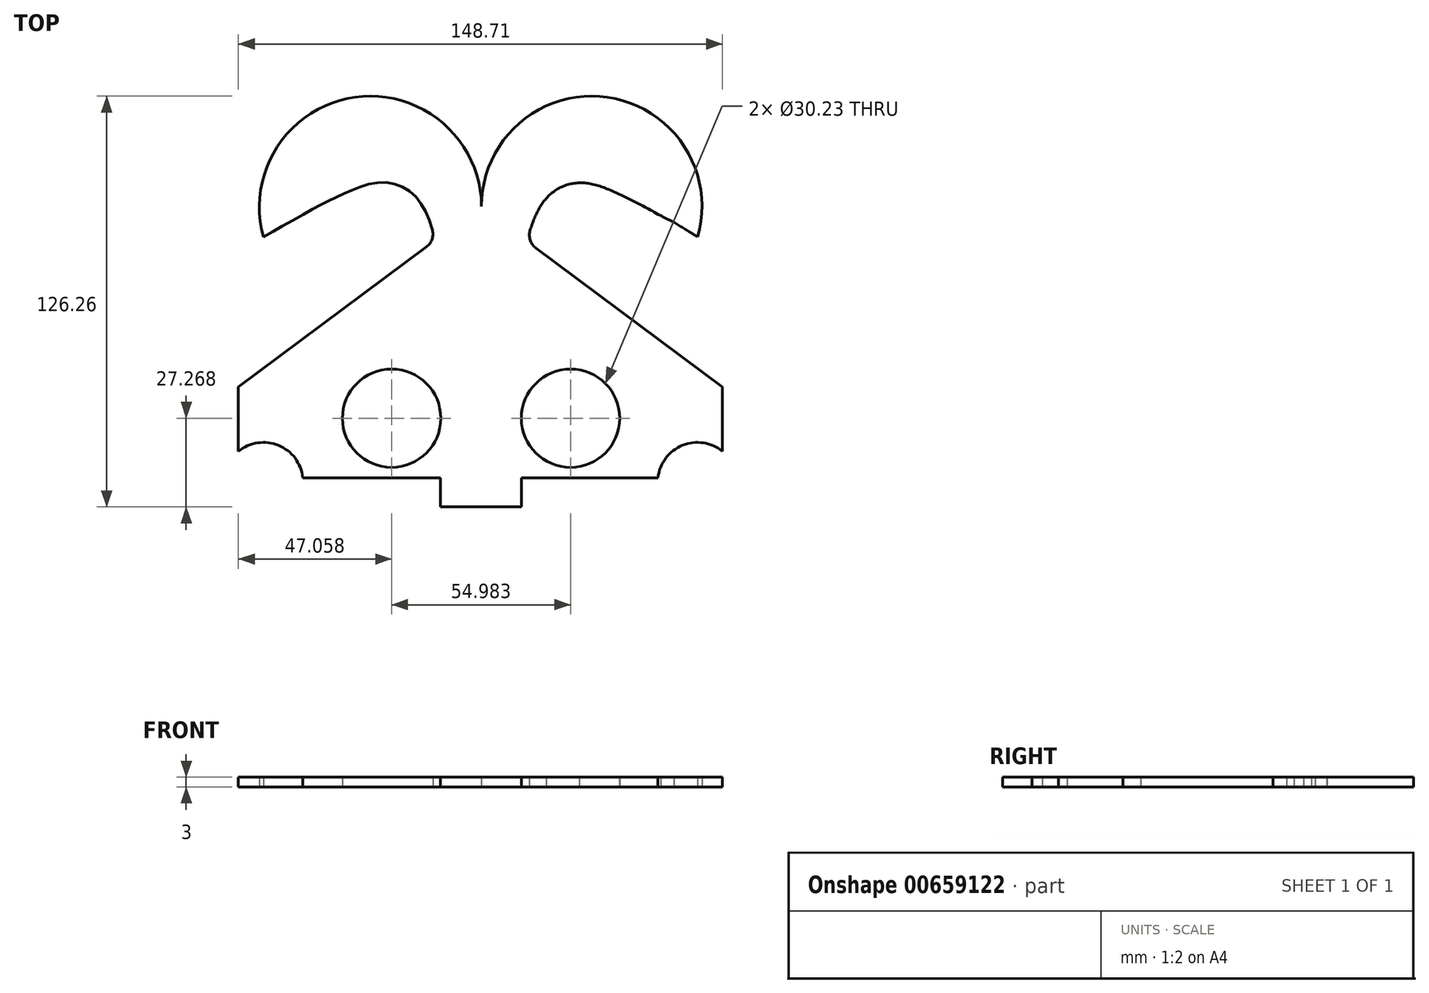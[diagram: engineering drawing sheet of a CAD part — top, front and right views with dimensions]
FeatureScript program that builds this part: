
annotation { "Feature Type Name" : "Feature", "Feature Type Description" : "" }
export const myFeature = defineFeature(function(context is Context, id is Id, definition is map)
    precondition{}
    {
        {
            var Q0;
            Q0=qCreatedBy(makeId("Top.planeOp"),FACE);
            var sketch = newSketch(context, id + "F0", { "sketchPlane" : qUnion([Q0])});
            skLineSegment(sketch, "E0", {"start": v(-16.81, 42.98) * mm, "end": v(-74.55, 0) * mm});
            skLineSegment(sketch, "E1", {"start": v(-74.55, 0) * mm, "end": v(-74.55, -19.8) * mm});
            skLineSegment(sketch, "E2", {"start": v(-54.75, -27.9) * mm, "end": v(0, -27.9) * mm});
            skLineSegment(sketch, "E3.MirrorCS", {"start": v(16.85, 42.67) * mm, "end": v(74.16, 0) * mm});
            skLineSegment(sketch, "E4.MirrorCS", {"start": v(54.36, -27.9) * mm, "end": v(-0.4, -27.9) * mm});
            skLineSegment(sketch, "E5.MirrorCS", {"start": v(74.16, 0) * mm, "end": v(74.16, -19.8) * mm});
            skArc(sketch, "E6", {"start": v(-54.75, -27.9) * mm, "mid": v(-62.25, -17.97) * mm, "end": v(-74.55, -19.8) * mm});
            skPoint(sketch, "E6.third.point", {"position": v(-77.85, -34.5) * mm});
            skPoint(sketch, "E7.MirrorP", {"position": v(77.46, -34.5) * mm});
            skArc(sketch, "E8.MirrorC", {"start": v(54.36, -27.9) * mm, "mid": v(61.85, -17.97) * mm, "end": v(74.16, -19.8) * mm});
            skLineSegment(sketch, "E9", {"start": v(0, -36.9) * mm, "end": v(-12.45, -36.9) * mm});
            skLineSegment(sketch, "E10", {"start": v(-12.45, -36.9) * mm, "end": v(-12.45, -27.9) * mm});
            skLineSegment(sketch, "E11.MirrorCS", {"start": v(12.45, -36.9) * mm, "end": v(12.45, -27.9) * mm});
            skLineSegment(sketch, "E12", {"start": v(0, -36.9) * mm, "end": v(12.45, -36.9) * mm});
            skPoint(sketch, "E13.start.orphan", {"position": v(0, 55.5) * mm});
            skLineSegment(sketch, "E14", {"start": v(0, 55.5) * mm, "end": v(0.14, 55.5) * mm});
            skArc(sketch, "E15", {"start": v(0.13, 55.5) * mm, "mid": v(-38.76, 89) * mm, "end": v(-66.88, 46.05) * mm});
            skArc(sketch, "E16", {"start": v(66.53, 46.1) * mm, "mid": v(38.75, 89.03) * mm, "end": v(0.14, 55.5) * mm});
            skPoint(sketch, "E17", {"position": v(-44.16, 22.63) * mm});
            skPoint(sketch, "E18", {"position": v(43.33, 22.95) * mm});
            skPoint(sketch, "E19", {"position": v(-66.88, 46.05) * mm});
            skPoint(sketch, "E20", {"position": v(66.52, 46.05) * mm});
            skPoint(sketch, "E21.start.orphan", {"position": v(34, 44.79) * mm});
            skFitSpline(sketch, "E22", {"points": [v(-14, 45.08) * mm, v(-19.7, 58.01) * mm, v(-29.9, 62.84) * mm, v(-42.25, 59.35) * mm, v(-54.87, 52.91) * mm, v(-66.88, 46.05) * mm, v(-59.17, 50.76) * mm], "startDerivative": vector(-23.96, 81.26) * mm, "endDerivative": vector(83.85, 50.75) * mm});
            skFitSpline(sketch, "E23.MirrorCS", {"points": [v(14.22, 45) * mm, v(20, 57.91) * mm, v(30.22, 62.7) * mm, v(42.55, 59.14) * mm, v(55.13, 52.63) * mm, v(67.1, 45.72) * mm, v(59.42, 50.47) * mm], "startDerivative": vector(24.37, 81.14) * mm, "endDerivative": vector(-83.6, 51.17) * mm});
            skLineSegment(sketch, "E24", {"start": v(0, -9.36) * mm, "end": v(-11.92, -9.36) * mm});
            skLineSegment(sketch, "E25", {"start": v(-11.92, -9.36) * mm, "end": v(12.23, -9.36) * mm});
            skPoint(sketch, "E26.start.orphan", {"position": v(-11.92, 0) * mm});
            skPoint(sketch, "E27.center.orphan", {"position": v(-27.5, 0) * mm});
            skCircle(sketch, "E28", {"center": v(-27.5, -9.63) * mm, "radius": 15.11 * mm});
            skCircle(sketch, "E29.MirrorC", {"center": v(27.5, -9.63) * mm, "radius": 15.11 * mm});
            skArc(sketch, "E30.filletArc", {"start": v(-16.81, 42.98) * mm, "mid": v(-15.04, 45.46) * mm, "end": v(-15.04, 48.5) * mm});
            skLineSegment(sketch, "E31", {"start": v(0.14, 55.5) * mm, "end": v(0, 0) * mm});
            skFitSpline(sketch, "E32", {"points": [v(14, 44.79) * mm, v(20, 57.91) * mm, v(30.22, 62.7) * mm, v(42.55, 59.14) * mm, v(55.13, 52.63) * mm, v(59.42, 50.47) * mm], "startDerivative": vector(19.83, 64.63) * mm, "endDerivative": vector(28.07, -13.85) * mm});
            skArc(sketch, "E33.filletArc", {"start": v(15.09, 48.24) * mm, "mid": v(15.07, 45.17) * mm, "end": v(16.85, 42.67) * mm});
            skSolve(sketch);
        }
        {
            var Q0;
            Q0=makeQuery(id+"F0.imprint","IMPRINT",FACE,{"disambiguationData":[TD([[makeQuery(id+"F0.imprint","IMPRINT",EDGE,{"derivedFrom":sQuery(id+"F0.wireOp",EDGE,"E9")}),-1.0]])]});
            var Q1;
            {var subQ0=sQuery(id+"F0.wireOp",EDGE,"E22");var subQ1=sQuery(id+"F0.wireOp",EDGE,"E15");var subQ2=makeQuery(id+"F0.imprint","INTERSECT",VERTEX,{"disambiguationData":[OD(0.0)],"derivedFrom":[subQ1,subQ0]});Q1=makeQuery(id+"F0.imprint","IMPRINT",FACE,{"disambiguationData":[TD([[makeQuery(id+"F0.imprint","IMPRINT",EDGE,{"disambiguationData":[TD([[subQ2,1.0]])],"derivedFrom":subQ1}),-1.0]])]});}
            var Q2;
            Q2=makeQuery(id+"F0.imprint","IMPRINT",FACE,{"disambiguationData":[TD([[makeQuery(id+"F0.imprint","IMPRINT",EDGE,{"derivedFrom":sQuery(id+"F0.wireOp",EDGE,"E0")}),1.0]])]});
            extrude(context, id + "F1", {"entities" : qUnion([Q0, Q1, Q2]), "depth" : 3 * mm, "offsetDistance" : 25 * mm});
        }
    });
